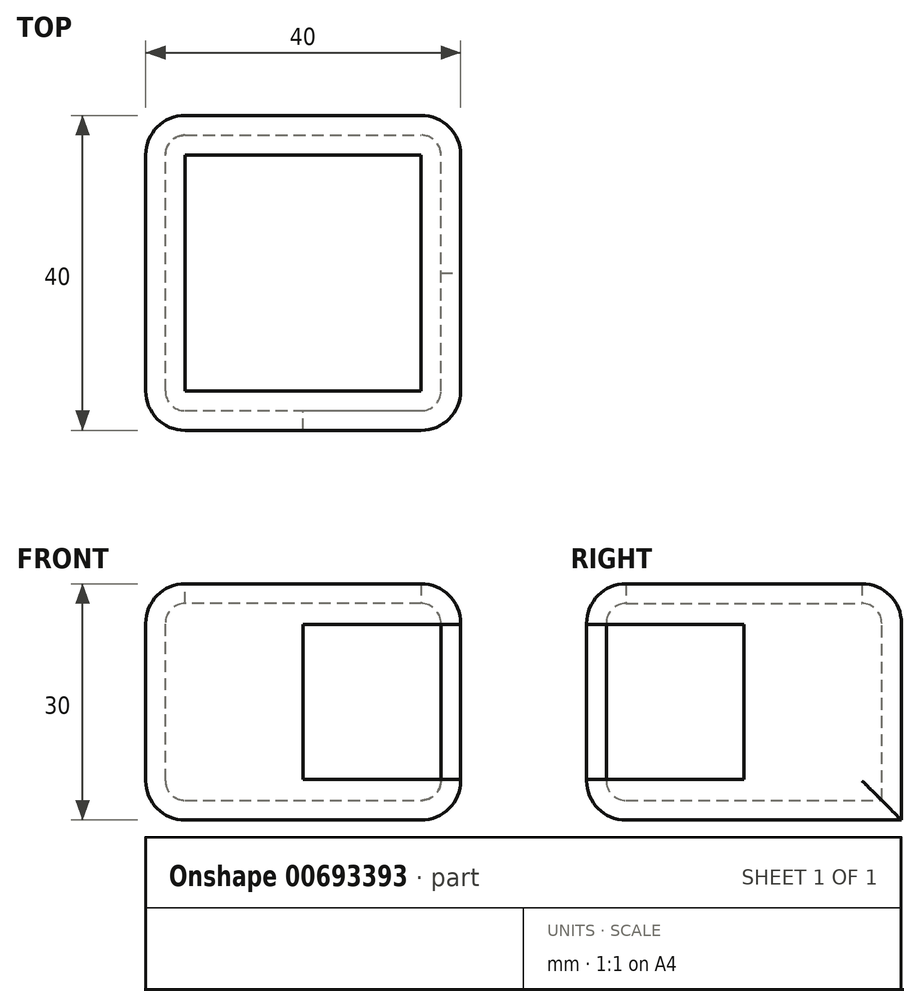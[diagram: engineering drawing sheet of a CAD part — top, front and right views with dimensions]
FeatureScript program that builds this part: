
annotation { "Feature Type Name" : "Feature", "Feature Type Description" : "" }
export const myFeature = defineFeature(function(context is Context, id is Id, definition is map)
    precondition{}
    {
        {
            var Q0;
            Q0=qCreatedBy(makeId("Top.planeOp"),FACE);
            var sketch = newSketch(context, id + "F0", { "sketchPlane" : qUnion([Q0])});
            skLineSegment(sketch, "E0.bottom", {"start": v(-20, -20) * mm, "end": v(20, -20) * mm});
            skLineSegment(sketch, "E0.top", {"start": v(-20, 20) * mm, "end": v(20, 20) * mm});
            skLineSegment(sketch, "E0.left", {"start": v(-20, -20) * mm, "end": v(-20, 20) * mm});
            skLineSegment(sketch, "E0.right", {"start": v(20, -20) * mm, "end": v(20, 20) * mm});
            skSolve(sketch);
        }
        {
            var Q0;
            Q0 = qSketchRegion(id + "F0", true);
            extrude(context, id + "F1", {"entities" : qUnion([Q0]), "depth" : 30 * mm, "offsetDistance" : 25 * mm});
        }
        {
            var Q0;
            Q0=makeQuery(id+"F1.opExtrude","SWEPT_FACE",FACE,{"disambiguationData":[OSD([sQuery(id+"F0.wireOp",EDGE,"E0.bottom")])]});
            var Q1;
            Q1=makeQuery(id+"F1.opExtrude","CAP_FACE",FACE,{"disambiguationData":[OSD([sQuery(id+"F0.wireOp",EDGE,"E0.bottom"),sQuery(id+"F0.wireOp",EDGE,"E0.top"),sQuery(id+"F0.wireOp",EDGE,"E0.left"),sQuery(id+"F0.wireOp",EDGE,"E0.right")])],"isStart":false});
            var Q2;
            Q2=makeQuery(id+"F1.opExtrude","SWEPT_FACE",FACE,{"disambiguationData":[OSD([sQuery(id+"F0.wireOp",EDGE,"E0.right")])]});
            var Q3;
            Q3=makeQuery(id+"F1.opExtrude","SWEPT_FACE",FACE,{"disambiguationData":[OSD([sQuery(id+"F0.wireOp",EDGE,"E0.left")])]});
            fillet(context, id + "F2", {"entities" : qUnion([Q0, Q1, Q2, Q3]), "radius" : 5 * mm, "tangentPropagation" : true, "allowEdgeOverflow" : false});
        }
        {
            var Q0;
            Q0=makeQuery(id+"F1.opExtrude","CAP_FACE",FACE,{"disambiguationData":[OSD([sQuery(id+"F0.wireOp",EDGE,"E0.bottom"),sQuery(id+"F0.wireOp",EDGE,"E0.top"),sQuery(id+"F0.wireOp",EDGE,"E0.left"),sQuery(id+"F0.wireOp",EDGE,"E0.right")])],"isStart":false});
            shell(context, id + "F3", {"entities" : qUnion([Q0]), "thickness" : 2.5 * mm});
        }
        {
            var Q0;
            Q0=qCreatedBy(makeId("Front.planeOp"),FACE);
            var sketch = newSketch(context, id + "F4", { "sketchPlane" : qUnion([Q0])});
            skLineSegment(sketch, "E1.bottom", {"start": v(0, 5.15) * mm, "end": v(20.26, 5.15) * mm});
            skLineSegment(sketch, "E1.top", {"start": v(0, 24.84) * mm, "end": v(20.26, 24.84) * mm});
            skLineSegment(sketch, "E1.left", {"start": v(0, 5.15) * mm, "end": v(0, 24.84) * mm});
            skLineSegment(sketch, "E1.right", {"start": v(20.26, 5.15) * mm, "end": v(20.26, 24.84) * mm});
            skSolve(sketch);
        }
        {
            var Q0;
            Q0 = qSketchRegion(id + "F4", true);
            extrude(context, id + "F5", {"entities" : qUnion([Q0]), "operationType" : NewBodyOperationType.REMOVE, "depth" : 61 * mm, "offsetDistance" : 25 * mm});
        }
    });
